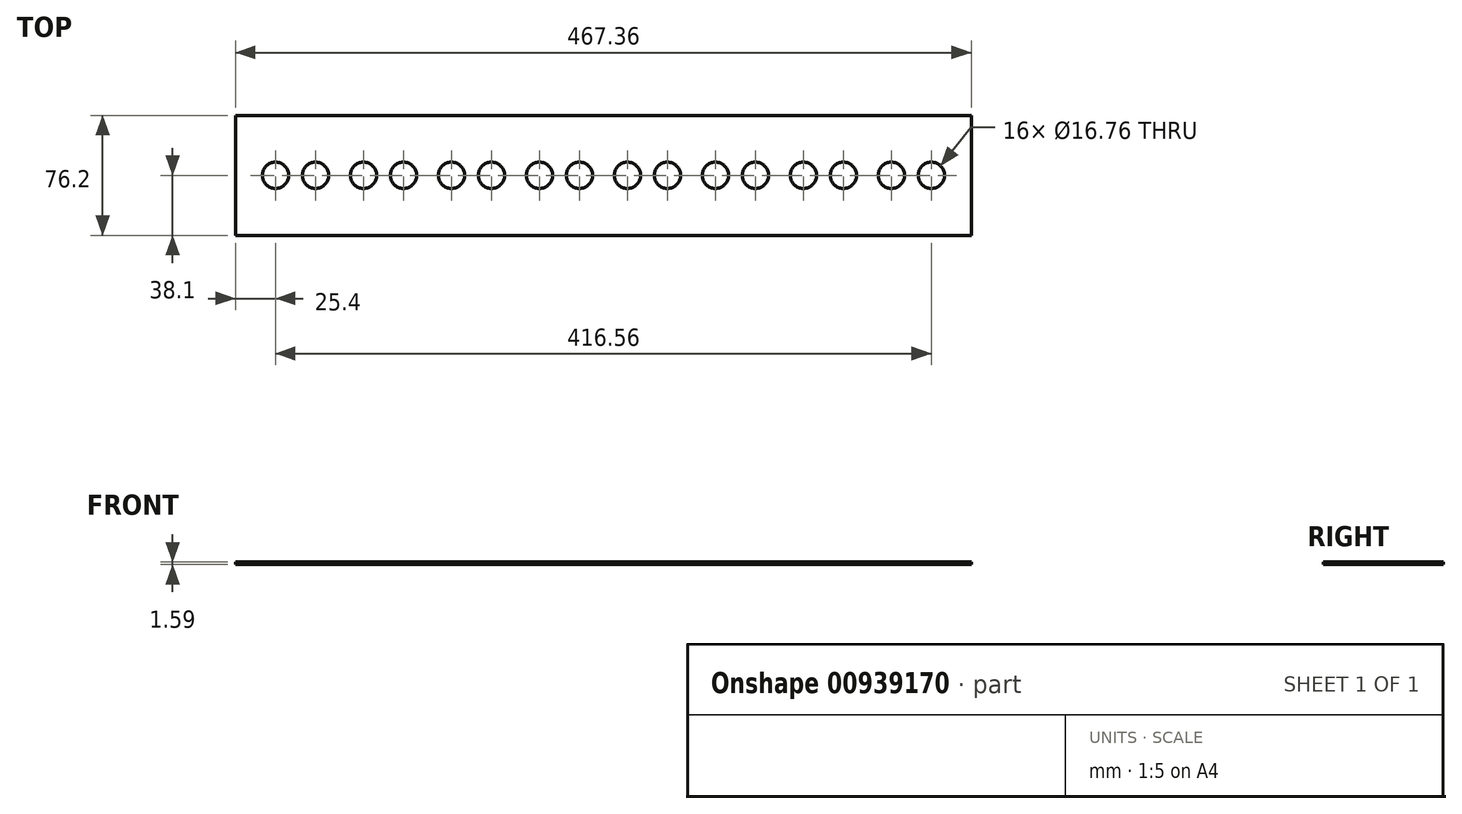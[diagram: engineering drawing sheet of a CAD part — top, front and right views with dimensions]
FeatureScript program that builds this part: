
annotation { "Feature Type Name" : "Feature", "Feature Type Description" : "" }
export const myFeature = defineFeature(function(context is Context, id is Id, definition is map)
    precondition{}
    {
        {
            var Q0;
            Q0=qCreatedBy(makeId("Top.planeOp"),FACE);
            var sketch = newSketch(context, id + "F0", { "sketchPlane" : qUnion([Q0])});
            skLineSegment(sketch, "E0.bottom", {"start": v(0, 0) * mm, "end": v(-467.36, 0) * mm});
            skLineSegment(sketch, "E0.top", {"start": v(0, 76.2) * mm, "end": v(-467.36, 76.2) * mm});
            skLineSegment(sketch, "E0.left", {"start": v(0, 0) * mm, "end": v(0, 76.2) * mm});
            skLineSegment(sketch, "E0.right", {"start": v(-467.36, 0) * mm, "end": v(-467.36, 76.2) * mm});
            skLineSegment(sketch, "E1", {"start": v(-467.36, 38.1) * mm, "end": v(0, 38.1) * mm, "construction": true});
            skLineSegment(sketch, "E2", {"start": v(-441.96, 76.2) * mm, "end": v(-441.96, 0) * mm, "construction": true});
            skLineSegment(sketch, "E3", {"start": v(-416.56, 128.54) * mm, "end": v(-416.56, 0) * mm, "construction": true});
            skLineSegment(sketch, "E4", {"start": v(-386.08, 76.2) * mm, "end": v(-386.08, 0) * mm, "construction": true});
            skLineSegment(sketch, "E5", {"start": v(-360.68, 76.2) * mm, "end": v(-360.68, 0) * mm, "construction": true});
            skLineSegment(sketch, "E6", {"start": v(-330.2, 76.2) * mm, "end": v(-330.2, 0) * mm, "construction": true});
            skLineSegment(sketch, "E7", {"start": v(-304.8, 76.2) * mm, "end": v(-304.8, 0) * mm, "construction": true});
            skLineSegment(sketch, "E8", {"start": v(-274.32, 76.2) * mm, "end": v(-274.32, 0) * mm, "construction": true});
            skLineSegment(sketch, "E9", {"start": v(-248.92, 76.2) * mm, "end": v(-248.92, 0) * mm, "construction": true});
            skLineSegment(sketch, "E10", {"start": v(-218.44, 76.2) * mm, "end": v(-218.44, 0) * mm, "construction": true});
            skLineSegment(sketch, "E11", {"start": v(-193.04, 76.2) * mm, "end": v(-193.04, 0) * mm, "construction": true});
            skLineSegment(sketch, "E12", {"start": v(-162.56, 76.2) * mm, "end": v(-162.56, 0) * mm, "construction": true});
            skLineSegment(sketch, "E13", {"start": v(-137.16, 76.2) * mm, "end": v(-137.16, 0) * mm, "construction": true});
            skLineSegment(sketch, "E14", {"start": v(-106.68, 76.2) * mm, "end": v(-106.68, 0) * mm, "construction": true});
            skCircle(sketch, "E15", {"center": v(-441.96, 38.1) * mm, "radius": 8.38 * mm});
            skCircle(sketch, "E16", {"center": v(-416.56, 38.1) * mm, "radius": 8.38 * mm});
            skCircle(sketch, "E17", {"center": v(-386.08, 38.1) * mm, "radius": 8.38 * mm});
            skCircle(sketch, "E18", {"center": v(-360.68, 38.1) * mm, "radius": 8.38 * mm});
            skCircle(sketch, "E19", {"center": v(-330.2, 38.1) * mm, "radius": 8.38 * mm});
            skCircle(sketch, "E20", {"center": v(-304.8, 38.1) * mm, "radius": 8.38 * mm});
            skCircle(sketch, "E21", {"center": v(-274.32, 38.1) * mm, "radius": 8.38 * mm});
            skCircle(sketch, "E22", {"center": v(-248.92, 38.1) * mm, "radius": 8.38 * mm});
            skCircle(sketch, "E23", {"center": v(-218.44, 38.1) * mm, "radius": 8.38 * mm});
            skCircle(sketch, "E24", {"center": v(-193.04, 38.1) * mm, "radius": 8.38 * mm});
            skCircle(sketch, "E25", {"center": v(-162.56, 38.1) * mm, "radius": 8.38 * mm});
            skCircle(sketch, "E26", {"center": v(-137.16, 38.1) * mm, "radius": 8.38 * mm});
            skCircle(sketch, "E27", {"center": v(-106.68, 38.1) * mm, "radius": 8.38 * mm});
            skLineSegment(sketch, "E28", {"start": v(-81.28, 76.2) * mm, "end": v(-81.28, 0) * mm, "construction": true});
            skLineSegment(sketch, "E29", {"start": v(-50.8, 76.2) * mm, "end": v(-50.8, 0) * mm, "construction": true});
            skLineSegment(sketch, "E30", {"start": v(-25.4, 76.2) * mm, "end": v(-25.4, 0) * mm, "construction": true});
            skCircle(sketch, "E31", {"center": v(-81.28, 38.1) * mm, "radius": 8.38 * mm});
            skCircle(sketch, "E32", {"center": v(-50.8, 38.1) * mm, "radius": 8.38 * mm});
            skCircle(sketch, "E33", {"center": v(-25.4, 38.1) * mm, "radius": 8.38 * mm});
            skSolve(sketch);
        }
        {
            var Q0;
            Q0=makeQuery(id+"F0.imprint","IMPRINT",FACE,{"disambiguationData":[TD([[makeQuery(id+"F0.imprint","IMPRINT",EDGE,{"derivedFrom":sQuery(id+"F0.wireOp",EDGE,"E0.bottom")}),-1.0]])]});
            extrude(context, id + "F1", {"entities" : qUnion([Q0]), "depth" : 1.59 * mm, "offsetDistance" : 25.4 * mm});
        }
    });
